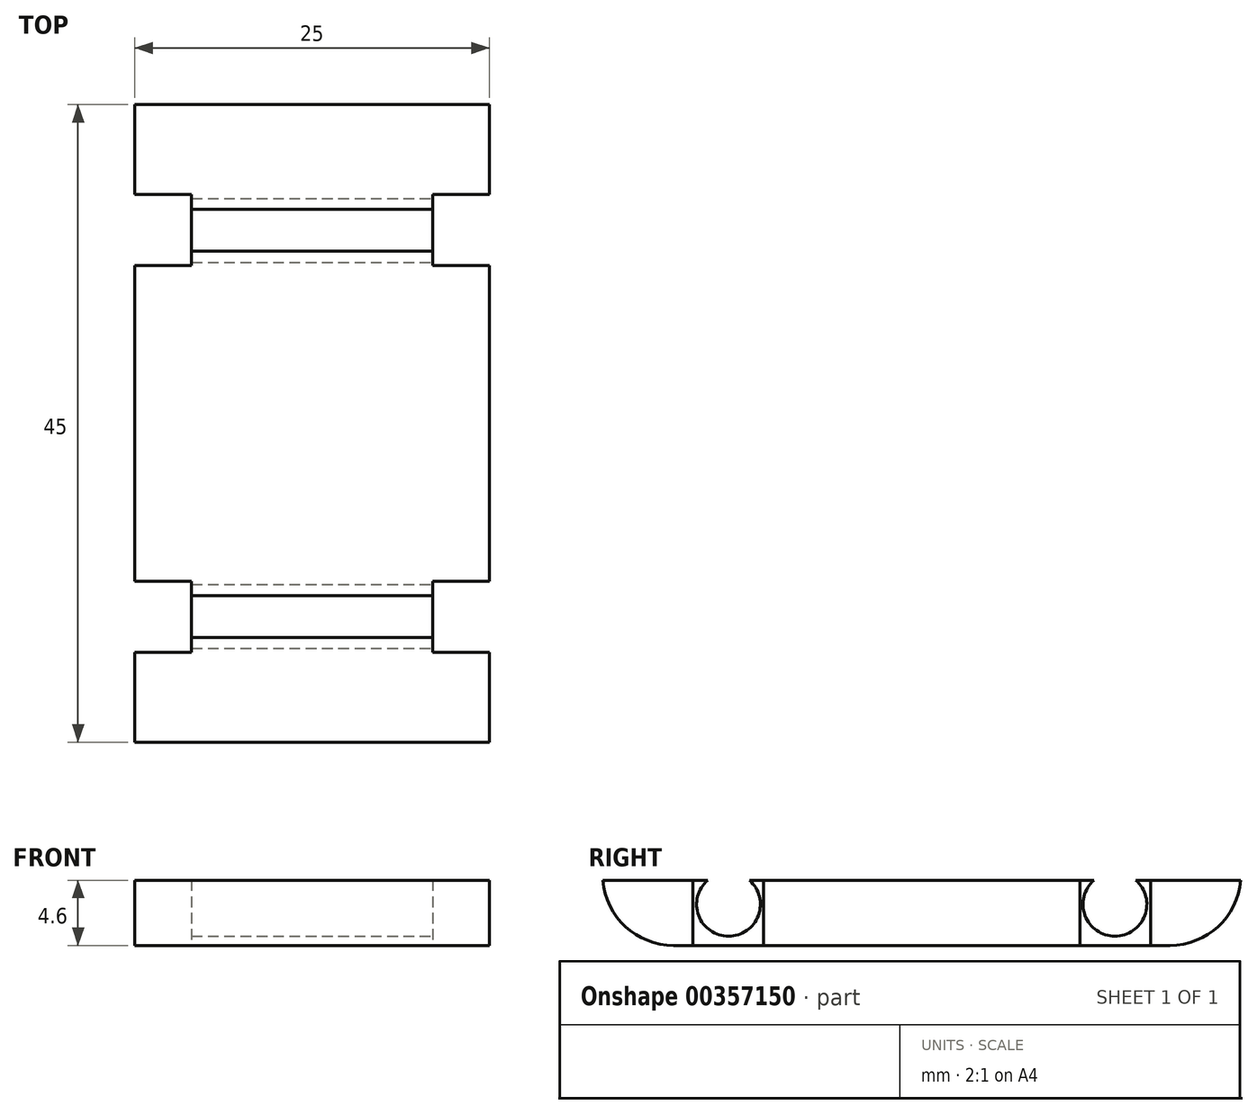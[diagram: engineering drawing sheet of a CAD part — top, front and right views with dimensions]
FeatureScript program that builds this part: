
annotation { "Feature Type Name" : "Feature", "Feature Type Description" : "" }
export const myFeature = defineFeature(function(context is Context, id is Id, definition is map)
    precondition{}
    {
        {
            var Q0;
            Q0=qCreatedBy(makeId("Top.planeOp"),FACE);
            var sketch = newSketch(context, id + "F0", { "sketchPlane" : qUnion([Q0])});
            skLineSegment(sketch, "E0.bottom", {"start": v(-12.5, 22.5) * mm, "end": v(12.5, 22.5) * mm});
            skLineSegment(sketch, "E0.top", {"start": v(-12.5, -22.5) * mm, "end": v(12.5, -22.5) * mm});
            skLineSegment(sketch, "E0.left", {"start": v(-12.5, 22.5) * mm, "end": v(-12.5, 16.15) * mm});
            skLineSegment(sketch, "E0.right", {"start": v(12.5, 22.5) * mm, "end": v(12.5, 16.15) * mm});
            skPoint(sketch, "E0.middle", {"position": v(0, 0) * mm});
            skLineSegment(sketch, "E1.bottom", {"start": v(-12.5, 16.15) * mm, "end": v(-8.5, 16.15) * mm});
            skLineSegment(sketch, "E1.top", {"start": v(-12.5, 11.15) * mm, "end": v(-8.5, 11.15) * mm});
            skLineSegment(sketch, "E1.right", {"start": v(-8.5, 16.15) * mm, "end": v(-8.5, 11.15) * mm});
            skLineSegment(sketch, "E2.trimOffspring", {"start": v(-12.5, 11.15) * mm, "end": v(-12.5, -11.15) * mm});
            skLineSegment(sketch, "E3.MirrorCS", {"start": v(12.5, 16.15) * mm, "end": v(8.5, 16.15) * mm});
            skLineSegment(sketch, "E4.MirrorCS", {"start": v(8.5, 16.15) * mm, "end": v(8.5, 11.15) * mm});
            skLineSegment(sketch, "E5.MirrorCS", {"start": v(12.5, 11.15) * mm, "end": v(8.5, 11.15) * mm});
            skLineSegment(sketch, "E6.MirrorCS", {"start": v(12.5, -11.15) * mm, "end": v(8.5, -11.15) * mm});
            skLineSegment(sketch, "E7.MirrorCS", {"start": v(8.5, -16.15) * mm, "end": v(8.5, -11.15) * mm});
            skLineSegment(sketch, "E8.MirrorCS", {"start": v(12.5, -16.15) * mm, "end": v(8.5, -16.15) * mm});
            skLineSegment(sketch, "E9.MirrorCS", {"start": v(-12.5, -11.15) * mm, "end": v(-8.5, -11.15) * mm});
            skLineSegment(sketch, "E10.MirrorCS", {"start": v(-8.5, -16.15) * mm, "end": v(-8.5, -11.15) * mm});
            skLineSegment(sketch, "E11.MirrorCS", {"start": v(-12.5, -16.15) * mm, "end": v(-8.5, -16.15) * mm});
            skLineSegment(sketch, "E12.trimOffspring", {"start": v(-12.5, -16.15) * mm, "end": v(-12.5, -22.5) * mm});
            skLineSegment(sketch, "E13.trimOffspring", {"start": v(12.5, -16.15) * mm, "end": v(12.5, -22.5) * mm});
            skLineSegment(sketch, "E14.trimOffspring", {"start": v(12.5, 11.15) * mm, "end": v(12.5, -11.15) * mm});
            skSolve(sketch);
        }
        {
            var Q0;
            Q0=makeQuery(id+"F0.imprint","IMPRINT",FACE,{"disambiguationData":[TD([[makeQuery(id+"F0.imprint","IMPRINT",EDGE,{"derivedFrom":sQuery(id+"F0.wireOp",EDGE,"E0.bottom")}),-1.0]])]});
            extrude(context, id + "F1", {"entities" : qUnion([Q0]), "endBound" : BoundingType.SYMMETRIC, "depth" : 4.6 * mm});
        }
        {
            var Q0;
            Q0=makeQuery(id+"F1.opExtrude","SWEPT_FACE",FACE,{"disambiguationData":[OSD([sQuery(id+"F0.wireOp",EDGE,"E7.MirrorCS")])]});
            var sketch = newSketch(context, id + "F2", { "sketchPlane" : qUnion([Q0])});
            skCircle(sketch, "E15", {"center": v(-13.63, 0.6) * mm, "radius": 2.25 * mm});
            skCircle(sketch, "E16.MirrorC", {"center": v(13.63, 0.6) * mm, "radius": 2.25 * mm});
            skSolve(sketch);
        }
        {
            var Q0;
            Q0 = qSketchRegion(id + "F2", true);
            extrude(context, id + "F3", {"entities" : qUnion([Q0]), "operationType" : NewBodyOperationType.REMOVE, "oppositeDirection" : true, "depth" : 25 * mm});
        }
        {
            var Q0;
            Q0=makeQuery(id+"F1.opExtrude","CAP_EDGE",EDGE,{"disambiguationData":[OSD([sQuery(id+"F0.wireOp",EDGE,"E0.top")])],"isStart":true});
            var Q1;
            Q1=makeQuery(id+"F1.opExtrude","CAP_EDGE",EDGE,{"disambiguationData":[OSD([sQuery(id+"F0.wireOp",EDGE,"E0.bottom")])],"isStart":true});
            fillet(context, id + "F4", {"entities" : qUnion([Q0, Q1]), "radius" : 5 * mm, "tangentPropagation" : true, "allowEdgeOverflow" : false});
        }
    });
